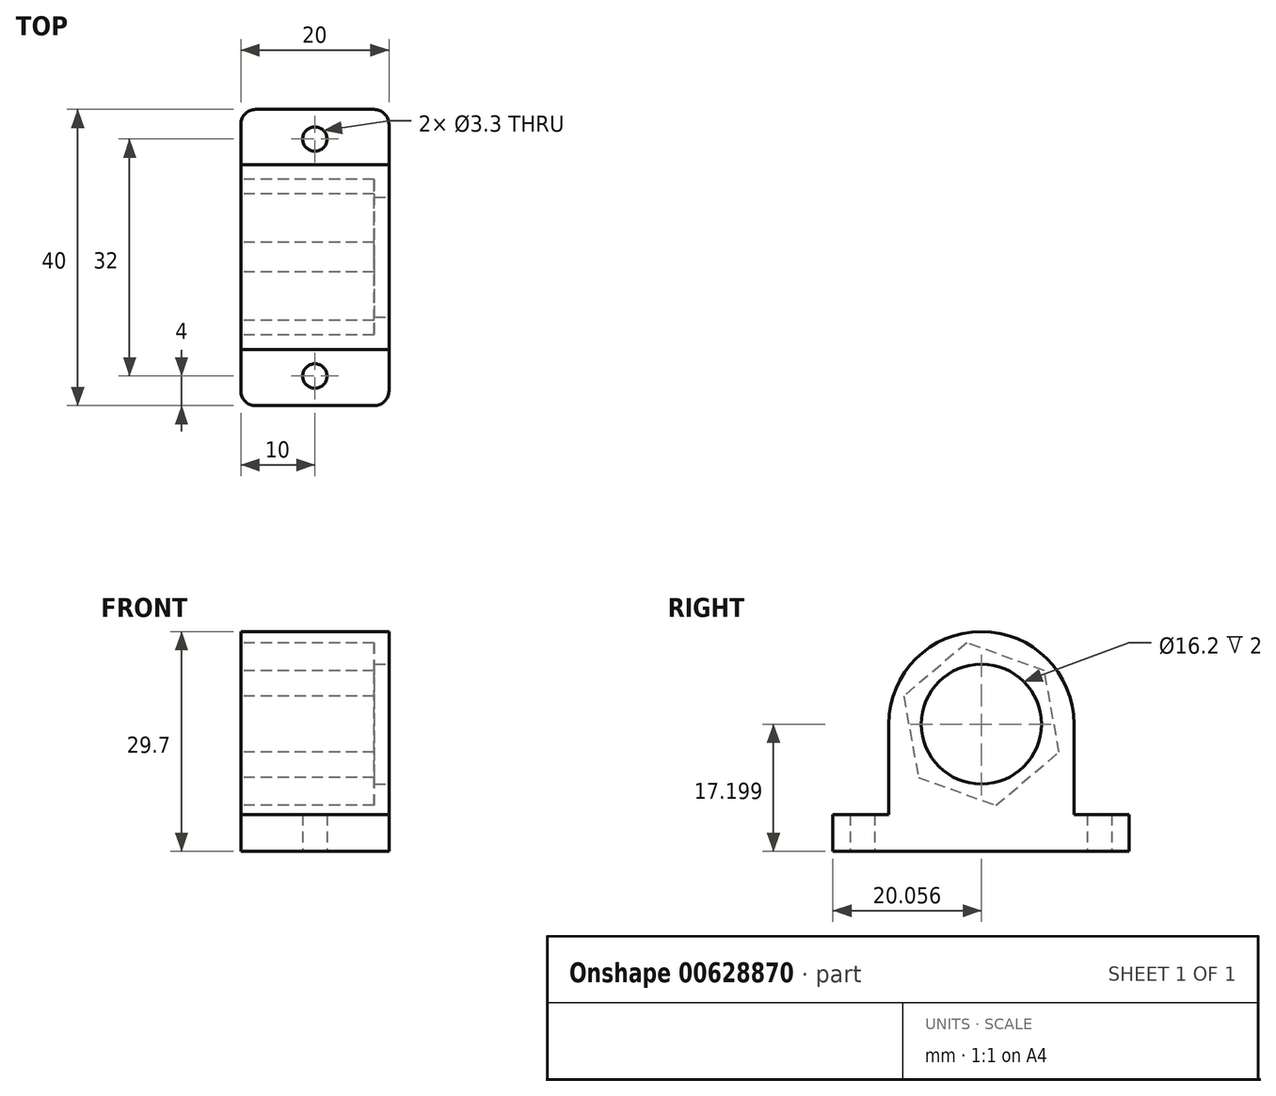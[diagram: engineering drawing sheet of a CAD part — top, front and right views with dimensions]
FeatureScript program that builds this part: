
annotation { "Feature Type Name" : "Feature", "Feature Type Description" : "" }
export const myFeature = defineFeature(function(context is Context, id is Id, definition is map)
    precondition{}
    {
        {
            var Q0;
            Q0=qCreatedBy(makeId("Top.planeOp"),FACE);
            var sketch = newSketch(context, id + "F0", { "sketchPlane" : qUnion([Q0])});
            skLineSegment(sketch, "E0.bottom", {"start": v(0, 0) * mm, "end": v(-20, 0) * mm});
            skLineSegment(sketch, "E0.top", {"start": v(0, 40) * mm, "end": v(-20, 40) * mm});
            skLineSegment(sketch, "E0.left", {"start": v(0, 0) * mm, "end": v(0, 40) * mm});
            skLineSegment(sketch, "E0.right", {"start": v(-20, 0) * mm, "end": v(-20, 40) * mm});
            skSolve(sketch);
        }
        {
            var Q0;
            Q0=qSketchRegion(id+"F0",true);
            var Q1;
            Q1=makeQuery(id+"F0.imprint","IMPRINT",FACE,{"disambiguationData":[TD([[makeQuery(id+"F0.imprint","IMPRINT",EDGE,{"derivedFrom":sQuery(id+"F0.wireOp",EDGE,"E0.bottom")}),-1.0]])]});
            extrude(context, id + "F1", {"entities" : qUnion([Q0, Q1]), "depth" : 5 * mm});
        }
        {
            var Q0;
            Q0=qCreatedBy(makeId("Right.planeOp"),FACE);
            var sketch = newSketch(context, id + "F2", { "sketchPlane" : qUnion([Q0])});
            skCircle(sketch, "E1", {"center": v(20.06, 17.2) * mm, "radius": 12.5 * mm});
            skLineSegment(sketch, "E2", {"start": v(5.36, 4.1) * mm, "end": v(32.34, 4.1) * mm});
            skCircle(sketch, "E3", {"center": v(20.06, 17.2) * mm, "radius": 8.1 * mm});
            skLineSegment(sketch, "E4", {"start": v(46.75, 17.2) * mm, "end": v(-10.52, 17.2) * mm, "construction": true});
            skLineSegment(sketch, "E5", {"start": v(32.56, 17.2) * mm, "end": v(32.56, 4.1) * mm});
            skLineSegment(sketch, "E6", {"start": v(7.56, 17.2) * mm, "end": v(7.56, 4.1) * mm});
            skLineSegment(sketch, "E7", {"start": v(32.34, 4.1) * mm, "end": v(32.56, 4.1) * mm});
            skSolve(sketch);
        }
        {
            var Q0;
            Q0=qSketchRegion(id+"F2",true);
            extrude(context, id + "F3", {"entities" : qUnion([Q0]), "operationType" : NewBodyOperationType.ADD, "oppositeDirection" : true, "depth" : 20 * mm});
        }
        {
            var Q0;
            Q0=makeQuery(id+"F3.boolean.opBoolean","MERGE",FACE,{"derivedFrom":[makeQuery(id+"F1.opExtrude","SWEPT_FACE",FACE,{"disambiguationData":[OSD([sQuery(id+"F0.wireOp",EDGE,"E0.right")])]}),makeQuery(id+"F3.opExtrude","CAP_FACE",FACE,{"disambiguationData":[OSD([sQuery(id+"F2.wireOp",EDGE,"E1"),sQuery(id+"F2.wireOp",EDGE,"9pyVx98I-oqo8-DIBG-djAO-6fVc5CMDMrcq"),sQuery(id+"F2.wireOp",EDGE,"E2"),sQuery(id+"F2.wireOp",EDGE,"dNc9zqT1-f1Ax-jlC8-ASgA-PEcgFVXjkpQC"),sQuery(id+"F2.wireOp",EDGE,"E3")])],"isStart":false})]});
            var sketch = newSketch(context, id + "F4", { "sketchPlane" : qUnion([Q0])});
            skCircle(sketch, "E8.cCircle", {"center": v(-20.06, 17.2) * mm, "radius": 9.65 * mm, "construction": true});
            skPoint(sketch, "E8.cCircle.perimeterSnap0", {"position": v(-32.2, 10.09) * mm});
            skLineSegment(sketch, "E8.0", {"start": v(-22.03, 6.23) * mm, "end": v(-30.54, 13.43) * mm});
            skLineSegment(sketch, "E8.1", {"start": v(-30.54, 13.43) * mm, "end": v(-28.57, 24.4) * mm});
            skLineSegment(sketch, "E8.2", {"start": v(-28.57, 24.4) * mm, "end": v(-18.08, 28.17) * mm});
            skLineSegment(sketch, "E8.3", {"start": v(-18.08, 28.17) * mm, "end": v(-9.57, 20.97) * mm});
            skLineSegment(sketch, "E8.4", {"start": v(-9.57, 20.97) * mm, "end": v(-11.55, 10) * mm});
            skLineSegment(sketch, "E8.5", {"start": v(-11.55, 10) * mm, "end": v(-22.03, 6.23) * mm});
            skPoint(sketch, "E8.0.midPoint", {"position": v(-26.29, 9.83) * mm});
            skPoint(sketch, "E8.0.midPoint.positionSnap0", {"position": v(-32.38, 9.83) * mm});
            skSolve(sketch);
        }
        {
            var Q0;
            Q0=qSketchRegion(id+"F4",true);
            extrude(context, id + "F5", {"entities" : qUnion([Q0]), "operationType" : NewBodyOperationType.REMOVE, "oppositeDirection" : true, "depth" : 18 * mm});
        }
        {
            var Q0;
            Q0=makeQuery(id+"F1.opExtrude","CAP_FACE",FACE,{"disambiguationData":[OSD([sQuery(id+"F0.wireOp",EDGE,"E0.bottom"),sQuery(id+"F0.wireOp",EDGE,"E0.top"),sQuery(id+"F0.wireOp",EDGE,"E0.left"),sQuery(id+"F0.wireOp",EDGE,"E0.right")])],"isStart":true});
            var sketch = newSketch(context, id + "F6", { "sketchPlane" : qUnion([Q0])});
            skLineSegment(sketch, "E9", {"start": v(0, -4) * mm, "end": v(-20, -4) * mm, "construction": true});
            skLineSegment(sketch, "E10", {"start": v(0, -36) * mm, "end": v(-20, -36) * mm, "construction": true});
            skLineSegment(sketch, "E11", {"start": v(-10, 0) * mm, "end": v(-10, -40) * mm, "construction": true});
            skCircle(sketch, "E12", {"center": v(-10, -4) * mm, "radius": 1.65 * mm});
            skCircle(sketch, "E13", {"center": v(-10, -36) * mm, "radius": 1.65 * mm});
            skSolve(sketch);
        }
        {
            var Q0;
            Q0=qSketchRegion(id+"F6",true);
            extrude(context, id + "F7", {"entities" : qUnion([Q0]), "operationType" : NewBodyOperationType.REMOVE, "endBound" : BoundingType.THROUGH_ALL, "oppositeDirection" : true, "depth" : 25 * mm});
        }
        {
            var Q0;
            Q0=makeQuery(id+"F1.opExtrude","SWEPT_EDGE",EDGE,{"disambiguationData":[OSD([sQuery(id+"F0.wireOp",EDGE,"E0.top"),sQuery(id+"F0.wireOp",EDGE,"E0.right")])]});
            var Q1;
            Q1=makeQuery(id+"F1.opExtrude","SWEPT_EDGE",EDGE,{"disambiguationData":[OSD([sQuery(id+"F0.wireOp",EDGE,"E0.top"),sQuery(id+"F0.wireOp",EDGE,"E0.left")])]});
            var Q2;
            Q2=makeQuery(id+"F1.opExtrude","SWEPT_EDGE",EDGE,{"disambiguationData":[OSD([sQuery(id+"F0.wireOp",EDGE,"E0.bottom"),sQuery(id+"F0.wireOp",EDGE,"E0.left")])]});
            var Q3;
            Q3=makeQuery(id+"F1.opExtrude","SWEPT_EDGE",EDGE,{"disambiguationData":[OSD([sQuery(id+"F0.wireOp",EDGE,"E0.bottom"),sQuery(id+"F0.wireOp",EDGE,"E0.right")])]});
            fillet(context, id + "F8", {"entities" : qUnion([Q0, Q1, Q2, Q3]), "radius" : 2 * mm, "tangentPropagation" : true, "allowEdgeOverflow" : false});
        }
    });
